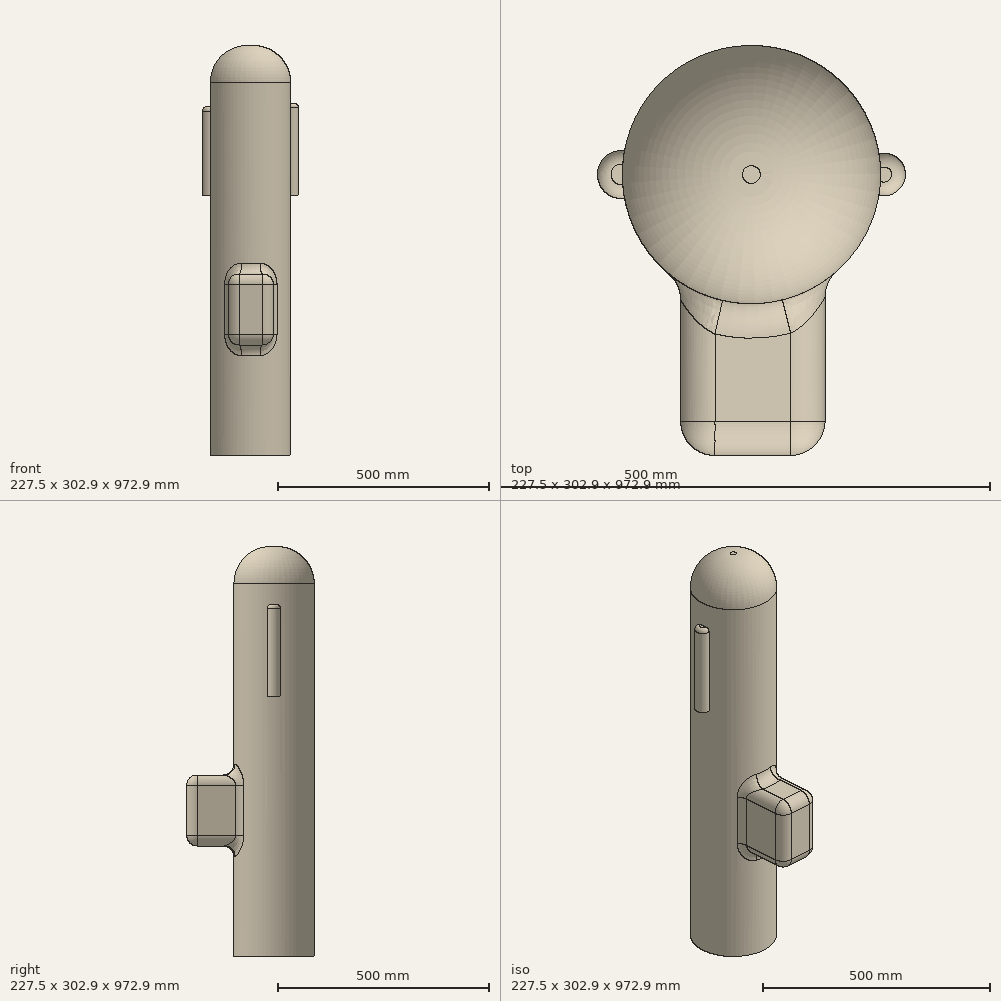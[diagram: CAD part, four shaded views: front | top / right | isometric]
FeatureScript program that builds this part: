
annotation { "Feature Type Name" : "Feature", "Feature Type Description" : "" }
export const myFeature = defineFeature(function(context is Context, id is Id, definition is map)
    precondition{}
    {
        {
            var Q0;
            Q0=qCreatedBy(makeId("Top.planeOp"),FACE);
            var sketch = newSketch(context, id + "F0", { "sketchPlane" : qUnion([Q0])});
            skCircle(sketch, "E0", {"center": v(0, 0) * mm, "radius": 95.43 * mm});
            skSolve(sketch);
        }
        {
            var Q0;
            Q0=makeQuery(id+"F0.imprint","IMPRINT",FACE,{"disambiguationData":[TD([[makeQuery(id+"F0.imprint","IMPRINT",EDGE,{"derivedFrom":sQuery(id+"F0.wireOp",EDGE,"E0")}),1.0]])]});
            extrude(context, id + "F1", {"entities" : qUnion([Q0]), "depth" : 356.67 * mm, "offsetDistance" : 25.4 * mm});
        }
        {
            var Q0;
            Q0=makeQuery(id+"F1.opExtrude","CAP_FACE",FACE,{"disambiguationData":[OSD([sQuery(id+"F0.wireOp",EDGE,"E0")])],"isStart":true});
            extrude(context, id + "F2", {"entities" : qUnion([Q0]), "operationType" : NewBodyOperationType.ADD, "depth" : 483.74 * mm, "offsetDistance" : 25.4 * mm});
        }
        {
            var Q0;
            Q0=makeQuery(id+"F1.opExtrude","CAP_EDGE",EDGE,{"disambiguationData":[OSD([sQuery(id+"F0.wireOp",EDGE,"E0")])],"isStart":false});
            fillet(context, id + "F3", {"entities" : qUnion([Q0]), "radius" : 88.9 * mm, "tangentPropagation" : true, "allowEdgeOverflow" : false});
        }
        {
            var Q0;
            Q0=qCreatedBy(makeId("Front.planeOp"),FACE);
            var sketch = newSketch(context, id + "F4", { "sketchPlane" : qUnion([Q0])});
            skLineSegment(sketch, "E1.bottom", {"start": v(-52.36, -185.6) * mm, "end": v(54.38, -185.6) * mm});
            skLineSegment(sketch, "E1.top", {"start": v(-52.36, -354.05) * mm, "end": v(54.38, -354.05) * mm});
            skLineSegment(sketch, "E1.left", {"start": v(-52.36, -185.6) * mm, "end": v(-52.36, -354.05) * mm});
            skLineSegment(sketch, "E1.right", {"start": v(54.38, -185.6) * mm, "end": v(54.38, -354.05) * mm});
            skSolve(sketch);
        }
        {
            var Q0;
            Q0 = qSketchRegion(id + "F4", true);
            extrude(context, id + "F5", {"entities" : qUnion([Q0]), "operationType" : NewBodyOperationType.ADD, "depth" : 207.5 * mm, "offsetDistance" : 25.4 * mm});
        }
        {
            var Q0;
            Q0=makeQuery(id+"F5.opExtrude","SWEPT_FACE",FACE,{"disambiguationData":[OSD([sQuery(id+"F4.wireOp",EDGE,"E1.bottom")])]});
            var Q1;
            Q1=makeQuery(id+"F5.opExtrude","SWEPT_FACE",FACE,{"disambiguationData":[OSD([sQuery(id+"F4.wireOp",EDGE,"E1.left")])]});
            var Q2;
            Q2=makeQuery(id+"F5.opExtrude","SWEPT_FACE",FACE,{"disambiguationData":[OSD([sQuery(id+"F4.wireOp",EDGE,"E1.right")])]});
            var Q3;
            Q3=makeQuery(id+"F5.opExtrude","SWEPT_FACE",FACE,{"disambiguationData":[OSD([sQuery(id+"F4.wireOp",EDGE,"E1.top")])]});
            fillet(context, id + "F6", {"entities" : qUnion([Q0, Q1, Q2, Q3]), "radius" : 25.4 * mm, "tangentPropagation" : true, "allowEdgeOverflow" : false});
        }
        {
            var Q0;
            Q0=makeQuery(id+"F2.opExtrude","CAP_FACE",FACE,{"disambiguationData":[OSD([sQuery(id+"F0.wireOp",EDGE,"E0")])],"isStart":false});
            shell(context, id + "F7", {"entities" : qUnion([Q0]), "thickness" : 2.54 * mm});
        }
        {
            var Q0;
            Q0=qCreatedBy(makeId("Front.planeOp"),FACE);
            var sketch = newSketch(context, id + "F8", { "sketchPlane" : qUnion([Q0])});
            skLineSegment(sketch, "E2.bottom", {"start": v(98.05, 0) * mm, "end": v(113.78, 0) * mm});
            skLineSegment(sketch, "E2.top", {"start": v(98.05, 219.66) * mm, "end": v(113.78, 219.66) * mm});
            skLineSegment(sketch, "E2.left", {"start": v(98.05, 0) * mm, "end": v(98.05, 219.66) * mm});
            skLineSegment(sketch, "E2.right", {"start": v(113.78, 0) * mm, "end": v(113.78, 219.66) * mm});
            skSolve(sketch);
        }
        {
            var Q0;
            Q0=qCreatedBy(makeId("Front.planeOp"),FACE);
            var sketch = newSketch(context, id + "F9", { "sketchPlane" : qUnion([Q0])});
            skLineSegment(sketch, "E3.bottom", {"start": v(-96, 0) * mm, "end": v(-113.76, 0) * mm});
            skLineSegment(sketch, "E3.top", {"start": v(-96, 211.11) * mm, "end": v(-113.76, 211.11) * mm});
            skLineSegment(sketch, "E3.left", {"start": v(-96, 0) * mm, "end": v(-96, 211.11) * mm});
            skLineSegment(sketch, "E3.right", {"start": v(-113.76, 0) * mm, "end": v(-113.76, 211.11) * mm});
            skSolve(sketch);
        }
        {
            var Q0;
            Q0=makeQuery(id+"F9.imprint","IMPRINT",FACE,{"disambiguationData":[TD([[makeQuery(id+"F9.imprint","IMPRINT",EDGE,{"derivedFrom":sQuery(id+"F9.wireOp",EDGE,"E3.bottom")}),-1.0]])]});
            var Q1;
            Q1=sQuery(id+"F9.wireOp",EDGE,"E3.left");
            revolve(context, id + "F10", {"operationType" : NewBodyOperationType.ADD, "entities" : qUnion([Q0]), "axis" : qUnion([Q1]), "revolveType" : RevolveType.FULL});
        }
        {
            var Q0;
            Q0=makeQuery(id+"F8.imprint","IMPRINT",FACE,{"disambiguationData":[TD([[makeQuery(id+"F8.imprint","IMPRINT",EDGE,{"derivedFrom":sQuery(id+"F8.wireOp",EDGE,"E2.bottom")}),1.0]])]});
            var Q1;
            Q1=sQuery(id+"F8.wireOp",EDGE,"E2.left");
            revolve(context, id + "F11", {"operationType" : NewBodyOperationType.ADD, "entities" : qUnion([Q0]), "axis" : qUnion([Q1]), "revolveType" : RevolveType.FULL});
        }
        {
            var Q0;
            {var subQ0=sQuery(id+"F0.wireOp",EDGE,"E0");var subQ1=sQuery(id+"F9.wireOp",EDGE,"E3.top");var subQ2=sQuery(id+"F9.wireOp",EDGE,"E3.right");Q0=makeQuery(id+"F10.boolean.opBoolean","SPLIT",EDGE,{"disambiguationData":[TD([makeQuery(id+"F1.opExtrude","SWEPT_FACE",FACE,{"disambiguationData":[OSD([subQ0])]})])],"derivedFrom":makeQuery(id+"F10.opRevolve","SWEPT_EDGE",EDGE,{"disambiguationData":[OSD([subQ1,subQ2])]})});}
            var Q1;
            {var subQ0=sQuery(id+"F0.wireOp",EDGE,"E0");var subQ1=sQuery(id+"F8.wireOp",EDGE,"E2.top");var subQ2=sQuery(id+"F8.wireOp",EDGE,"E2.right");Q1=makeQuery(id+"F11.boolean.opBoolean","SPLIT",EDGE,{"disambiguationData":[TD([makeQuery(id+"F1.opExtrude","SWEPT_FACE",FACE,{"disambiguationData":[OSD([subQ0])]})])],"derivedFrom":makeQuery(id+"F11.opRevolve","SWEPT_EDGE",EDGE,{"disambiguationData":[OSD([subQ1,subQ2])]})});}
            fillet(context, id + "F12", {"entities" : qUnion([Q0, Q1]), "radius" : 10.16 * mm, "tangentPropagation" : true, "allowEdgeOverflow" : false});
        }
        {
            var Q0;
            Q0=makeQuery(id+"F2.opExtrude","CAP_FACE",FACE,{"disambiguationData":[OSD([sQuery(id+"F0.wireOp",EDGE,"E0")])],"isStart":false});
            extrude(context, id + "F13", {"entities" : qUnion([Q0]), "operationType" : NewBodyOperationType.ADD, "depth" : 132.53 * mm, "offsetDistance" : 25.4 * mm});
        }
    });
